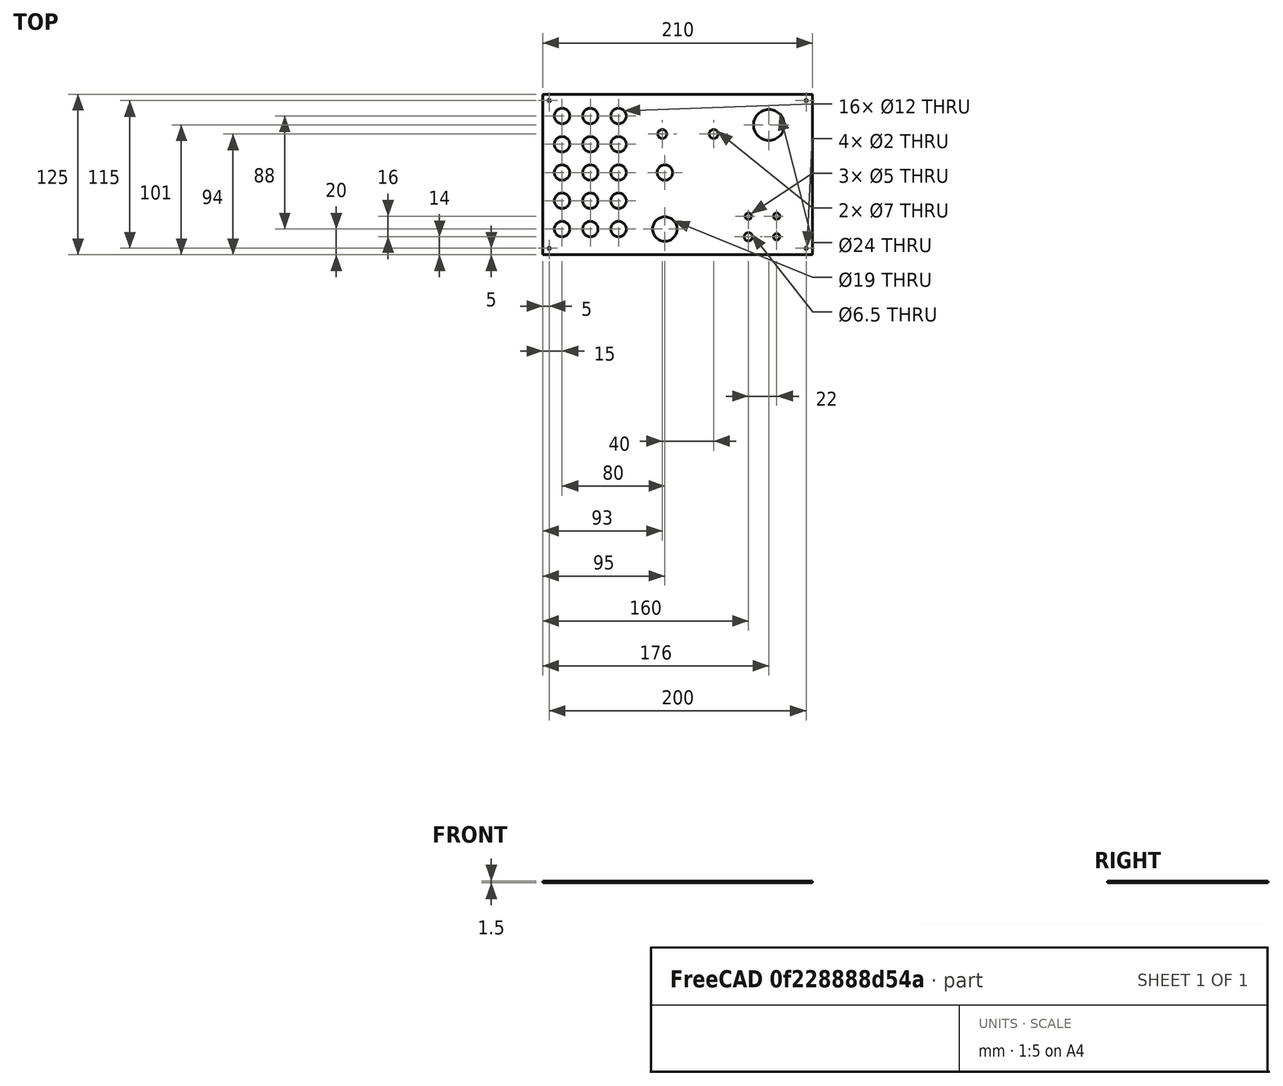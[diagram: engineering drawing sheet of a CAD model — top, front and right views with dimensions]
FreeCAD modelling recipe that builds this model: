
FCSTD DOCUMENT  (FreeCAD 0.19R24276 (Git))
Label: frontplatte_ats_ets
License: All rights reserved
LicenseURL: http://en.wikipedia.org/wiki/All_rights_reserved
objects: TechDraw::DrawViewDimension×5, Sketcher::SketchObject×1, PartDesign::Pad×1, PartDesign::Body×1, TechDraw::DrawSVGTemplate×1, TechDraw::DrawProjGroupItem×1, TechDraw::DrawProjGroup×1, TechDraw::DrawPage×1
note: 4 computed .brp shape members not serialized (recipe doc carries the construction recipe); baked Part::Feature solids carry a one-line shape summary decoded from their .brp

FEATURE [Sketcher::SketchObject] Sketch
  FullyConstrained = true
  MapMode = 5
  Support = -> [XY_Plane]
  sketch-geometry (65):
    g0: LineSegment StartX=0 StartY=125 StartZ=0 EndX=210 EndY=125 EndZ=0
    g1: LineSegment StartX=210 StartY=125 StartZ=0 EndX=210 EndY=0 EndZ=0
    g2: LineSegment StartX=210 StartY=0 StartZ=0 EndX=0 EndY=0 EndZ=0
    g3: LineSegment StartX=0 StartY=0 StartZ=0 EndX=0 EndY=125 EndZ=0
    g4: Circle CenterX=15 CenterY=108 CenterZ=0 NormalX=0 NormalY=0 NormalZ=1 AngleXU=0 Radius=6
    g5: Circle CenterX=15 CenterY=86 CenterZ=0 NormalX=0 NormalY=0 NormalZ=1 AngleXU=0 Radius=6
    g6: Circle CenterX=15 CenterY=64 CenterZ=0 NormalX=0 NormalY=0 NormalZ=1 AngleXU=0 Radius=6
    g7: LineSegment StartX=15 StartY=108 StartZ=0 EndX=15 EndY=86 EndZ=0
    g8: LineSegment StartX=15 StartY=86 StartZ=0 EndX=15 EndY=64 EndZ=0
    g9: Circle CenterX=15 CenterY=42 CenterZ=0 NormalX=0 NormalY=0 NormalZ=1 AngleXU=0 Radius=6
    g10: LineSegment StartX=15 StartY=64 StartZ=0 EndX=15 EndY=42 EndZ=0
    g11: Circle CenterX=15 CenterY=20 CenterZ=0 NormalX=0 NormalY=0 NormalZ=1 AngleXU=0 Radius=6
    g12: LineSegment StartX=15 StartY=42 StartZ=0 EndX=15 EndY=20 EndZ=0
    g13: Circle CenterX=176 CenterY=101 CenterZ=0 NormalX=0 NormalY=0 NormalZ=1 AngleXU=0 Radius=12
    g14: Circle CenterX=182 CenterY=14 CenterZ=0 NormalX=0 NormalY=0 NormalZ=1 AngleXU=0 Radius=2.5
    g15: Circle CenterX=182 CenterY=30 CenterZ=0 NormalX=0 NormalY=0 NormalZ=1 AngleXU=0 Radius=2.5
    g16: LineSegment StartX=182 StartY=14 StartZ=0 EndX=182 EndY=30 EndZ=0
    g17: Circle CenterX=160 CenterY=30 CenterZ=0 NormalX=0 NormalY=0 NormalZ=1 AngleXU=0 Radius=2.5
    g18: Circle CenterX=160 CenterY=14 CenterZ=0 NormalX=0 NormalY=0 NormalZ=1 AngleXU=0 Radius=3.25
    g19: LineSegment StartX=182 StartY=30 StartZ=0 EndX=160 EndY=30 EndZ=0
    g20: LineSegment StartX=182 StartY=14 StartZ=0 EndX=160 EndY=14 EndZ=0
    g21: LineSegment StartX=160 StartY=30 StartZ=0 EndX=160 EndY=14 EndZ=0
    g22: Circle CenterX=95 CenterY=64 CenterZ=0 NormalX=0 NormalY=0 NormalZ=1 AngleXU=0 Radius=6
    g23: Circle CenterX=205 CenterY=120 CenterZ=0 NormalX=0 NormalY=0 NormalZ=1 AngleXU=0 Radius=1
    g24: Circle CenterX=37 CenterY=108 CenterZ=0 NormalX=0 NormalY=0 NormalZ=1 AngleXU=0 Radius=6
    g25: LineSegment StartX=15 StartY=108 StartZ=0 EndX=37 EndY=108 EndZ=0
    g26: Circle CenterX=37 CenterY=86 CenterZ=0 NormalX=0 NormalY=0 NormalZ=1 AngleXU=0 Radius=6
    g27: LineSegment StartX=37 StartY=108 StartZ=0 EndX=37 EndY=86 EndZ=0
    g28: LineSegment StartX=15 StartY=86 StartZ=0 EndX=37 EndY=86 EndZ=0
    g29: Circle CenterX=37 CenterY=64 CenterZ=0 NormalX=0 NormalY=0 NormalZ=1 AngleXU=0 Radius=6
    g30: LineSegment StartX=37 StartY=86 StartZ=0 EndX=37 EndY=64 EndZ=0
    g31: LineSegment StartX=15 StartY=64 StartZ=0 EndX=37 EndY=64 EndZ=0
    g32: Circle CenterX=37 CenterY=42 CenterZ=0 NormalX=0 NormalY=0 NormalZ=1 AngleXU=0 Radius=6
    g33: LineSegment StartX=15 StartY=42 StartZ=0 EndX=37 EndY=42 EndZ=0
    g34: LineSegment StartX=37 StartY=64 StartZ=0 EndX=37 EndY=42 EndZ=0
    g35: Circle CenterX=37 CenterY=20 CenterZ=0 NormalX=0 NormalY=0 NormalZ=1 AngleXU=0 Radius=6
    g36: LineSegment StartX=37 StartY=42 StartZ=0 EndX=37 EndY=20 EndZ=0
    g37: LineSegment StartX=15 StartY=20 StartZ=0 EndX=37 EndY=20 EndZ=0
    g38: Circle CenterX=59 CenterY=108 CenterZ=0 NormalX=0 NormalY=0 NormalZ=1 AngleXU=0 Radius=6
    g39: LineSegment StartX=37 StartY=108 StartZ=0 EndX=59 EndY=108 EndZ=0
    g40: Circle CenterX=59 CenterY=86 CenterZ=0 NormalX=0 NormalY=0 NormalZ=1 AngleXU=0 Radius=6
    g41: LineSegment StartX=37 StartY=86 StartZ=0 EndX=59 EndY=86 EndZ=0
    g42: LineSegment StartX=59 StartY=108 StartZ=0 EndX=59 EndY=86 EndZ=0
    g43: Circle CenterX=59 CenterY=64 CenterZ=0 NormalX=0 NormalY=0 NormalZ=1 AngleXU=0 Radius=6
    g44: LineSegment StartX=59 StartY=86 StartZ=0 EndX=59 EndY=64 EndZ=0
    g45: LineSegment StartX=37 StartY=64 StartZ=0 EndX=59 EndY=64 EndZ=0
    g46: Circle CenterX=59 CenterY=42 CenterZ=0 NormalX=0 NormalY=0 NormalZ=1 AngleXU=0 Radius=6
    g47: LineSegment StartX=37 StartY=42 StartZ=0 EndX=59 EndY=42 EndZ=0
    g48: LineSegment StartX=59 StartY=64 StartZ=0 EndX=59 EndY=42 EndZ=0
    g49: Circle CenterX=59 CenterY=20 CenterZ=0 NormalX=0 NormalY=0 NormalZ=1 AngleXU=0 Radius=6
    g50: LineSegment StartX=59 StartY=42 StartZ=0 EndX=59 EndY=20 EndZ=0
    g51: LineSegment StartX=37 StartY=20 StartZ=0 EndX=59 EndY=20 EndZ=0
    g52: Circle CenterX=95 CenterY=20 CenterZ=0 NormalX=0 NormalY=0 NormalZ=1 AngleXU=0 Radius=9.5
    g53: LineSegment StartX=95 StartY=64 StartZ=0 EndX=95 EndY=20 EndZ=0
    g54: LineSegment StartX=59 StartY=20 StartZ=0 EndX=95 EndY=20 EndZ=0
    g55: Circle CenterX=205 CenterY=5 CenterZ=0 NormalX=0 NormalY=0 NormalZ=1 AngleXU=0 Radius=1
    g56: LineSegment StartX=205 StartY=120 StartZ=0 EndX=205 EndY=5 EndZ=0
    g57: Circle CenterX=5 CenterY=5 CenterZ=0 NormalX=0 NormalY=0 NormalZ=1 AngleXU=0 Radius=1
    g58: LineSegment StartX=5 StartY=5 StartZ=0 EndX=205 EndY=5 EndZ=0
    g59: Circle CenterX=5 CenterY=120 CenterZ=0 NormalX=0 NormalY=0 NormalZ=1 AngleXU=0 Radius=1
    g60: LineSegment StartX=5 StartY=120 StartZ=0 EndX=5 EndY=5 EndZ=0
    g61: LineSegment StartX=5 StartY=120 StartZ=0 EndX=205 EndY=120 EndZ=0
    g62: Circle CenterX=93 CenterY=94 CenterZ=0 NormalX=0 NormalY=0 NormalZ=1 AngleXU=0 Radius=3.5
    g63: Circle CenterX=133 CenterY=94 CenterZ=0 NormalX=0 NormalY=0 NormalZ=1 AngleXU=0 Radius=3.5
    g64: LineSegment StartX=93 StartY=94 StartZ=0 EndX=133 EndY=94 EndZ=0
  constraints (161):
    c: Coincident(g0,g1)
    c: Coincident(g1,g2)
    c: Coincident(g2,g3)
    c: Coincident(g3,g0)
    c: Horizontal(g0)
    c: Horizontal(g2)
    c: Vertical(g1)
    c: Vertical(g3)
    c: Coincident(g2,g-1)
    c: DistanceY(g3,g3) = 125
    c: DistanceX(g2,g2) = 210
    c: Diameter(g4) = 12
    c: DistanceX(g0,g4) = 15
    c: Equal(g4,g5) = 12
    c: Coincident(g7,g4)
    c: Coincident(g7,g5)
    c: Vertical(g7)
    c: Coincident(g8,g5)
    c: Coincident(g8,g6)
    c: Vertical(g8)
    c: DistanceY(g2,g4) = 108
    c: DistanceY(g2,g5) = 86
    c: DistanceY(g2,g6) = 64
    c: Equal(g6,g5)
    c: Equal(g4,g9) = 12
    c: Coincident(g10,g6)
    c: Coincident(g10,g9)
    c: Vertical(g10)
    c: DistanceY(g2,g9) = 42
    c: DistanceY(g2,g11) = 20
    c: Coincident(g12,g9)
    c: Coincident(g12,g11)
    c: Vertical(g12)
    c: Equal(g11,g6)
    c: Diameter(g13) = 24
    c: DistanceX(g2,g13) = 176
    c: DistanceY(g1,g13) = 101
    c: DistanceY(g1,g14) = 14
    c: DistanceX(g2,g14) = 182
    c: Diameter(g14) = 5
    c: Equal(g14,g15) = 5
    c: Coincident(g16,g14)
    c: Coincident(g16,g15)
    c: Vertical(g16)
    c: DistanceY(g1,g15) = 30
    c: Diameter(g18) = 6.5
    c: Equal(g17,g15)
    c: DistanceX(g2,g18) = 160
    c: Coincident(g19,g15)
    c: Coincident(g19,g17)
    c: Horizontal(g19)
    c: Coincident(g20,g14)
    c: Coincident(g20,g18)
    c: Horizontal(g20)
    c: Coincident(g21,g17)
    c: Coincident(g21,g18)
    c: Vertical(g21)
    c: Diameter(g22) = 12
    c: DistanceX(g2,g22) = 95
    c: DistanceY(g1,g22) = 64
    c: Diameter(g23) = 2
    c: DistanceX(g23,g0) = 5
    c: DistanceY(g23,g0) = 5
    c: Equal(g4,g24) = 12
    c: DistanceX(g0,g24) = 37
    c: Coincident(g25,g4)
    c: Coincident(g25,g24)
    c: Horizontal(g25)
    c: Coincident(g27,g24)
    c: Coincident(g27,g26)
    c: Vertical(g27)
    c: Coincident(g28,g5)
    c: Coincident(g28,g26)
    c: Horizontal(g28)
    c: Coincident(g30,g26)
    c: Coincident(g30,g29)
    c: Vertical(g30)
    c: Coincident(g31,g6)
    c: Coincident(g31,g29)
    c: Horizontal(g31)
    c: Coincident(g33,g9)
    c: Coincident(g33,g32)
    c: Horizontal(g33)
    c: Coincident(g34,g29)
    c: Coincident(g34,g32)
    c: Vertical(g34)
    c: Coincident(g36,g32)
    c: Coincident(g36,g35)
    c: Vertical(g36)
    c: Coincident(g37,g11)
    c: Coincident(g37,g35)
    c: Horizontal(g37)
    c: Equal(g26,g29)
    c: Equal(g29,g32)
    c: Equal(g32,g35)
    c: Equal(g35,g24)
    c: DistanceX(g0,g38) = 59
    c: Coincident(g39,g24)
    c: Coincident(g39,g38)
    c: Horizontal(g39)
    c: Coincident(g41,g26)
    c: Coincident(g41,g40)
    c: Horizontal(g41)
    c: Coincident(g42,g38)
    c: Coincident(g42,g40)
    c: Vertical(g42)
    c: Coincident(g44,g40)
    c: Coincident(g44,g43)
    c: Vertical(g44)
    c: Coincident(g45,g29)
    c: Coincident(g45,g43)
    c: Horizontal(g45)
    c: Coincident(g47,g32)
    c: Coincident(g47,g46)
    c: Horizontal(g47)
    c: Coincident(g48,g43)
    c: Coincident(g48,g46)
    c: Vertical(g48)
    c: Coincident(g50,g46)
    c: Coincident(g50,g49)
    c: Vertical(g50)
    c: Coincident(g51,g35)
    c: Coincident(g51,g49)
    c: Horizontal(g51)
    c: Equal(g38,g40)
    c: Equal(g40,g43)
    c: Equal(g43,g46)
    c: Equal(g46,g49)
    c: Equal(g49,g24)
    c: Diameter(g52) = 19
    c: Coincident(g53,g22)
    c: Coincident(g53,g52)
    c: Vertical(g53)
    c: Coincident(g54,g49)
    c: Coincident(g54,g52)
    c: Horizontal(g54)
    c: Equal(g23,g55) = 2
    c: Coincident(g56,g23)
    c: Coincident(g56,g55)
    c: Vertical(g56)
    c: DistanceY(g1,g55) = 5
    c: Coincident(g58,g57)
    c: Coincident(g58,g55)
    c: Horizontal(g58)
    c: DistanceX(g2,g57) = 5
    c: Coincident(g60,g59)
    c: Coincident(g60,g57)
    c: Vertical(g60)
    c: Coincident(g61,g59)
    c: Coincident(g61,g23)
    c: Horizontal(g61)
    c: Equal(g59,g57)
    c: Equal(g57,g23)
    c: Coincident(g64,g62)
    c: Coincident(g64,g63)
    c: Horizontal(g64)
    c: DistanceX(g0,g62) = 93
    c: DistanceX(g0,g63) = 133
    c: DistanceY(g1,g63) = 94
    c: Diameter(g62) = 7
    c: Equal(g62,g63)
FEATURE [PartDesign::Pad] Pad
  Direction = (1,1,1)
  Length = 1.5
  Length2 = 100
  Profile = -> Sketch
  Refine = true
  Type = 0
FEATURE [PartDesign::Body] Body
  Group = -> [Sketch,Pad]
  Origin = -> Origin
  Tip = -> Pad
FEATURE [TechDraw::DrawSVGTemplate] Template
  EditableTexts = Designed_by_Name=R.Klose; FC-Date=2021-04-19; FC-SC=1:2; FC-SH=1; FC-Title=ATS ETS Frontblende V2.5
  Height = 210
  Orientation = 1
  Width = 297
FEATURE [TechDraw::DrawProjGroupItem] ProjItem  label="Front"
  CoarseView = false
  Direction = (0,0,1)
  Focus = 100
  HardHidden = false
  IsoCount = 0
  IsoHidden = false
  IsoVisible = false
  LockPosition = true
  Perspective = false
  Rotation = 0
  RotationVector = (1,0,0)
  Scale = 0.5
  ScaleType = 2
  SeamHidden = false
  SeamVisible = true
  SmoothHidden = false
  SmoothVisible = true
  Source = -> [Pad]
  Type = 0
  X = 0
  XDirection = (1,0,0)
  Y = 0
FEATURE [TechDraw::DrawProjGroup] ProjGroup
  Anchor = -> ProjItem
  AutoDistribute = true
  LockPosition = false
  ProjectionType = 0
  Rotation = 0
  Scale = 0.5
  ScaleType = 0
  Source = -> [Pad]
  Views = -> [ProjItem]
  X = 147.82
  Y = 130.485
  spacingX = 15
  spacingY = 15
FEATURE [TechDraw::DrawViewDimension] Dimension
  Arbitrary = false
  ArbitraryTolerances = false
  EqualTolerance = true
  FormatSpec = %.0f
  FormatSpecOverTolerance = %+.0f
  FormatSpecUnderTolerance = %+.0f
  Inverted = false
  LockPosition = false
  MeasureType = 1
  OverTolerance = 0
  References2D = -> [ProjItem]
  Rotation = 0
  Scale = 0.5
  ScaleType = 0
  TheoreticalExact = false
  Type = 2
  UnderTolerance = 0
  X = -65.4787
  Y = -0.707929
FEATURE [TechDraw::DrawViewDimension] Dimension001
  Arbitrary = false
  ArbitraryTolerances = false
  EqualTolerance = true
  FormatSpec = %.0f
  FormatSpecOverTolerance = %+.0f
  FormatSpecUnderTolerance = %+.0f
  Inverted = false
  LockPosition = false
  MeasureType = 1
  OverTolerance = 0
  References2D = -> [ProjItem]
  Rotation = 0
  Scale = 0.5
  ScaleType = 0
  TheoreticalExact = false
  Type = 1
  UnderTolerance = 0
  X = 0
  Y = -39.2732
FEATURE [TechDraw::DrawViewDimension] Dimension002
  Arbitrary = false
  ArbitraryTolerances = false
  EqualTolerance = true
  FormatSpec = ⌀%.0f
  FormatSpecOverTolerance = %+.0f
  FormatSpecUnderTolerance = %+.0f
  Inverted = false
  LockPosition = false
  MeasureType = 1
  OverTolerance = 0
  References2D = -> [ProjItem]
  Rotation = 0
  Scale = 0.5
  ScaleType = 0
  TheoreticalExact = false
  Type = 5
  UnderTolerance = 0
  X = 62.7697
  Y = 25.4854
FEATURE [TechDraw::DrawViewDimension] Dimension003
  Arbitrary = false
  ArbitraryTolerances = false
  EqualTolerance = true
  FormatSpec = ⌀%.0f
  FormatSpecOverTolerance = %+.0f
  FormatSpecUnderTolerance = %+.0f
  Inverted = false
  LockPosition = false
  MeasureType = 1
  OverTolerance = 0
  References2D = -> [ProjItem]
  Rotation = 0
  Scale = 0.5
  ScaleType = 0
  TheoreticalExact = false
  Type = 5
  UnderTolerance = 0
  X = -8.02319
  Y = 28.0812
FEATURE [TechDraw::DrawViewDimension] Dimension004
  Arbitrary = false
  ArbitraryTolerances = false
  EqualTolerance = true
  FormatSpec = ⌀%.0f
  FormatSpecOverTolerance = %+.0f
  FormatSpecUnderTolerance = %+.0f
  Inverted = false
  LockPosition = false
  MeasureType = 1
  OverTolerance = 0
  References2D = -> [ProjItem]
  Rotation = 0
  Scale = 0.5
  ScaleType = 0
  TheoreticalExact = false
  Type = 5
  UnderTolerance = 0
  X = 10.6189
  Y = 30.9129
FEATURE [TechDraw::DrawPage] Page
  KeepUpdated = true
  NextBalloonIndex = 1
  ProjectionType = 0
  Scale = 0.5
  Template = -> Template
  Views = -> [ProjGroup,Dimension,Dimension001,Dimension002,Dimension003,Dimension004]
